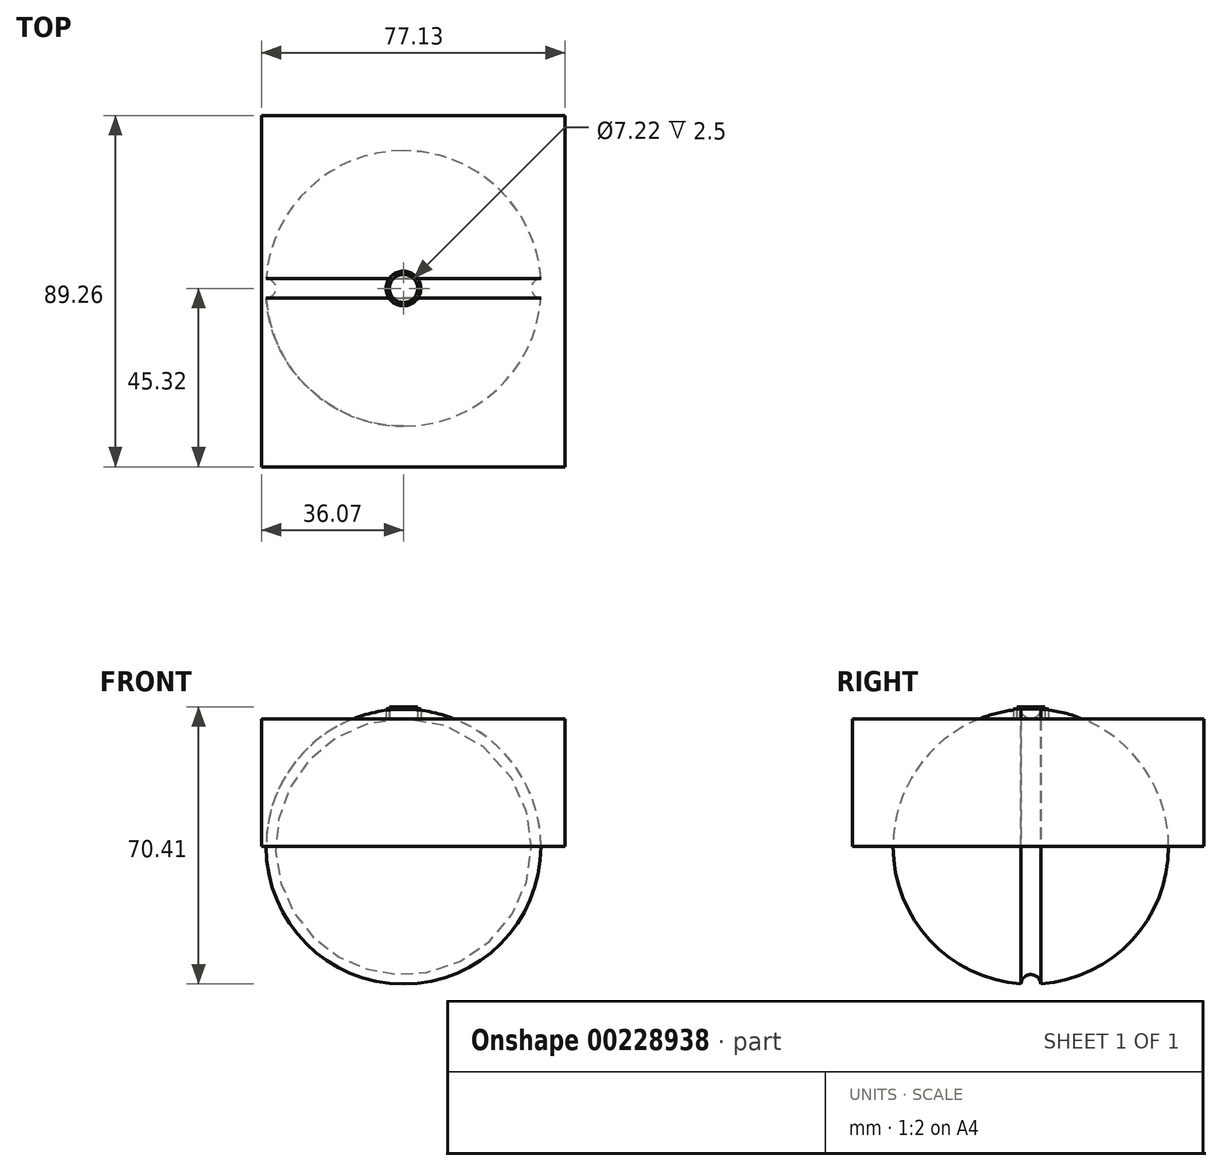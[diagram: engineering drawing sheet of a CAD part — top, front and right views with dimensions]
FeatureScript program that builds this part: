
annotation { "Feature Type Name" : "Feature", "Feature Type Description" : "" }
export const myFeature = defineFeature(function(context is Context, id is Id, definition is map)
    precondition{}
    {
        {
            var Q0;
            Q0=qCreatedBy(makeId("Top.planeOp"),FACE);
            var sketch = newSketch(context, id + "F0", { "sketchPlane" : qUnion([Q0])});
            skCircle(sketch, "E0", {"center": v(0, 0) * mm, "radius": 35 * mm});
            skLineSegment(sketch, "E1", {"start": v(0, 35) * mm, "end": v(0, -35) * mm});
            skCircle(sketch, "E2", {"center": v(-35, 0) * mm, "radius": 2.5 * mm});
            skSolve(sketch);
        }
        {
            var Q0;
            {var subQ0=sQuery(id+"F0.wireOp",EDGE,"E1");Q0=makeQuery(id+"F0.imprint","IMPRINT",FACE,{"disambiguationData":[TD([[makeQuery(id+"F0.imprint","IMPRINT",EDGE,{"derivedFrom":subQ0}),-1.0]])]});}
            var Q1;
            Q1=sQuery(id+"F0.wireOp",EDGE,"E1");
            revolve(context, id + "F1", {"entities" : qUnion([Q0]), "axis" : qUnion([Q1]), "revolveType" : RevolveType.FULL});
        }
        {
            var Q0;
            Q0=qCreatedBy(makeId("Top.planeOp"),FACE);
            var sketch = newSketch(context, id + "F2", { "sketchPlane" : qUnion([Q0])});
            skLineSegment(sketch, "E3.bottom", {"start": v(-36.07, 43.94) * mm, "end": v(41.06, 43.94) * mm});
            skLineSegment(sketch, "E3.top", {"start": v(-36.07, -45.32) * mm, "end": v(41.06, -45.32) * mm});
            skLineSegment(sketch, "E3.left", {"start": v(-36.07, 43.94) * mm, "end": v(-36.07, -45.32) * mm});
            skLineSegment(sketch, "E3.right", {"start": v(41.06, 43.94) * mm, "end": v(41.06, -45.32) * mm});
            skSolve(sketch);
        }
        {
            var Q0;
            Q0=makeQuery(id+"F2.imprint","IMPRINT",FACE,{"disambiguationData":[TD([[makeQuery(id+"F2.imprint","IMPRINT",EDGE,{"derivedFrom":sQuery(id+"F2.wireOp",EDGE,"E3.bottom")}),-1.0]])]});
            extrude(context, id + "F3", {"entities" : qUnion([Q0]), "depth" : 32.5 * mm});
        }
        {
            var Q0;
            Q0=makeQuery(id+"F3.opExtrude","CAP_FACE",FACE,{"disambiguationData":[OSD([sQuery(id+"F2.wireOp",EDGE,"E3.bottom"),sQuery(id+"F2.wireOp",EDGE,"E3.top"),sQuery(id+"F2.wireOp",EDGE,"E3.left"),sQuery(id+"F2.wireOp",EDGE,"E3.right")])],"isStart":false});
            var sketch = newSketch(context, id + "F4", { "sketchPlane" : qUnion([Q0])});
            skCircle(sketch, "E4", {"center": v(0, 0) * mm, "radius": 4.42 * mm});
            skCircle(sketch, "E5", {"center": v(0, 0) * mm, "radius": 3.61 * mm});
            skSolve(sketch);
        }
        {
            var Q0;
            Q0=makeQuery(id+"F4.imprint","IMPRINT",FACE,{"disambiguationData":[TD([[makeQuery(id+"F4.imprint","IMPRINT",EDGE,{"derivedFrom":sQuery(id+"F4.wireOp",EDGE,"E4")}),-1.0]])]});
            var sketch = newSketch(context, id + "F5", { "sketchPlane" : qUnion([Q0])});
            skCircle(sketch, "E6", {"center": v(0, 0) * mm, "radius": 3.59 * mm});
            skSolve(sketch);
        }
        {
            var Q0;
            Q0 = qSketchRegion(id + "F4", true);
            extrude(context, id + "F6", {"entities" : qUnion([Q0]), "depth" : 2.5 * mm});
        }
        {
            var Q0;
            Q0 = qSketchRegion(id + "F5", true);
            extrude(context, id + "F7", {"entities" : qUnion([Q0]), "depth" : 3 * mm});
        }
    });
